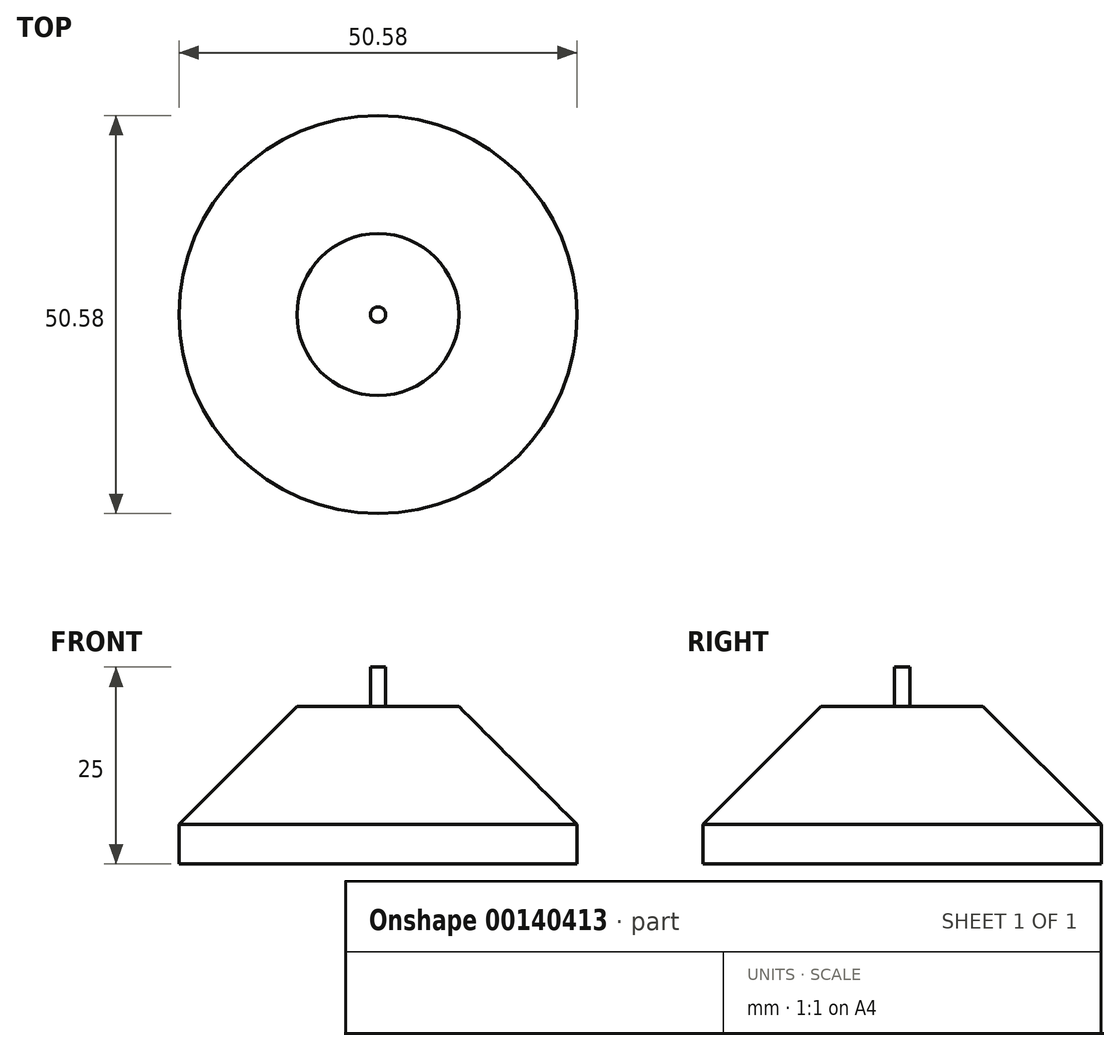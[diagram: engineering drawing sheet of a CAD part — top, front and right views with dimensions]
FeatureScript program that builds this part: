
annotation { "Feature Type Name" : "Feature", "Feature Type Description" : "" }
export const myFeature = defineFeature(function(context is Context, id is Id, definition is map)
    precondition{}
    {
        {
            var Q0;
            Q0=qCreatedBy(makeId("Top.planeOp"),FACE);
            var sketch = newSketch(context, id + "F0", { "sketchPlane" : qUnion([Q0])});
            skCircle(sketch, "E0", {"center": v(0, 0) * mm, "radius": 25.29 * mm});
            skCircle(sketch, "E1", {"center": v(0, 0) * mm, "radius": 0.98 * mm});
            skSolve(sketch);
        }
        {
            var Q0;
            Q0=makeQuery(id+"F0.imprint","IMPRINT",FACE,{"disambiguationData":[TD([[makeQuery(id+"F0.imprint","IMPRINT",EDGE,{"derivedFrom":sQuery(id+"F0.wireOp",EDGE,"E1")}),1.0]])]});
            extrude(context, id + "F1", {"entities" : qUnion([Q0]), "depth" : 25 * mm});
        }
        {
            var Q0;
            Q0 = qSketchRegion(id + "F0", true);
            extrude(context, id + "F2", {"entities" : qUnion([Q0]), "operationType" : NewBodyOperationType.ADD, "depth" : 20 * mm});
        }
        {
            var Q0;
            Q0=makeQuery(id+"F2.opExtrude","CAP_EDGE",EDGE,{"disambiguationData":[OSD([sQuery(id+"F0.wireOp",EDGE,"E0")])],"isStart":false});
            chamfer(context, id + "F3", {"entities" : qUnion([Q0]), "width" : 15 * mm, "tangentPropagation" : true});
        }
    });
